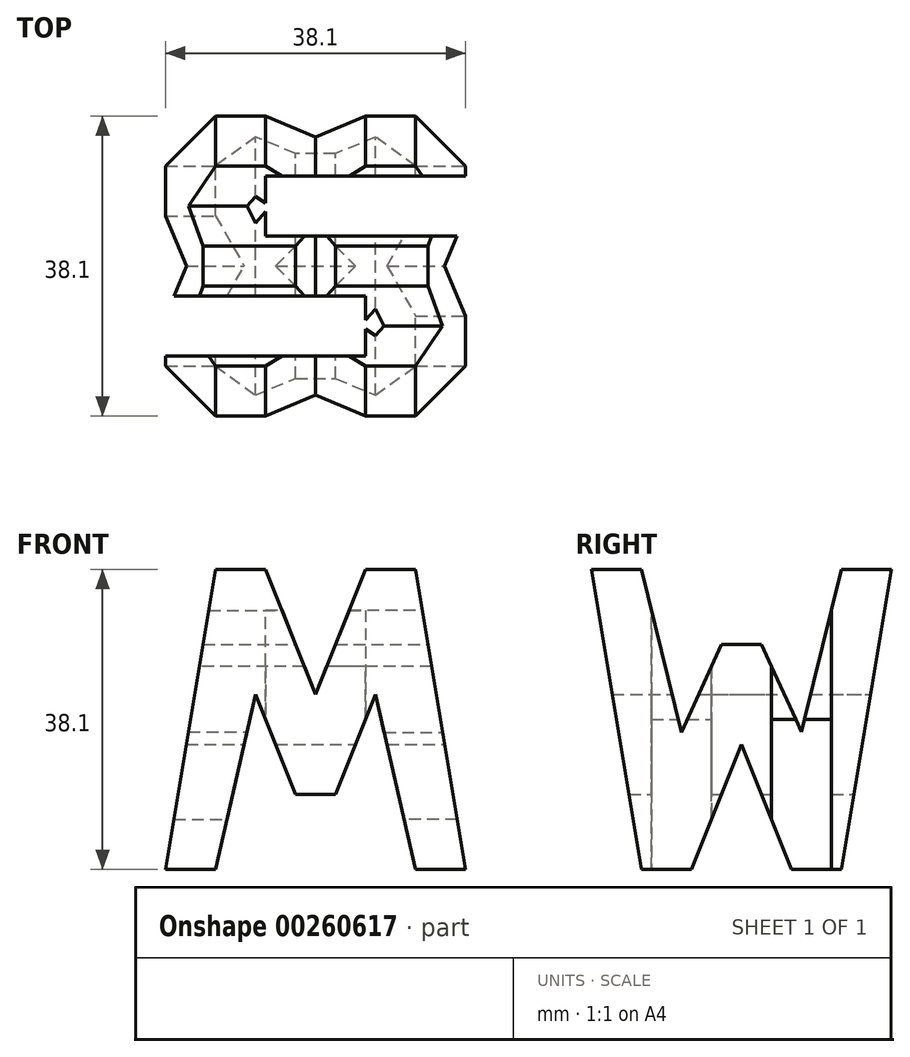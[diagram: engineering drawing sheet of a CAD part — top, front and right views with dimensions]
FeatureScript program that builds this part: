
annotation { "Feature Type Name" : "Feature", "Feature Type Description" : "" }
export const myFeature = defineFeature(function(context is Context, id is Id, definition is map)
    precondition{}
    {
        {
            var Q0;
            Q0=qCreatedBy(makeId("Front.planeOp"),FACE);
            var sketch = newSketch(context, id + "F0", { "sketchPlane" : qUnion([Q0])});
            skLineSegment(sketch, "E0", {"start": v(0, 0) * mm, "end": v(38.1, 0) * mm});
            skLineSegment(sketch, "E1", {"start": v(38.1, 0) * mm, "end": v(38.1, 38.1) * mm});
            skLineSegment(sketch, "E2", {"start": v(38.1, 38.1) * mm, "end": v(0, 38.1) * mm});
            skLineSegment(sketch, "E3", {"start": v(0, 38.1) * mm, "end": v(0, 0) * mm});
            skLineSegment(sketch, "E4", {"start": v(38.1, 0) * mm, "end": v(31.75, 38.1) * mm});
            skLineSegment(sketch, "E5", {"start": v(25.4, 38.1) * mm, "end": v(19.05, 22.22) * mm});
            skPoint(sketch, "E5.endSnap0", {"position": v(19.05, 38.1) * mm});
            skLineSegment(sketch, "E6", {"start": v(19.05, 22.22) * mm, "end": v(12.7, 38.1) * mm});
            skLineSegment(sketch, "E7", {"start": v(0, 0) * mm, "end": v(6.35, 38.1) * mm});
            skLineSegment(sketch, "E8", {"start": v(31.75, 0) * mm, "end": v(26.67, 22.23) * mm});
            skLineSegment(sketch, "E9", {"start": v(26.67, 22.23) * mm, "end": v(21.6, 9.52) * mm});
            skLineSegment(sketch, "E10", {"start": v(21.59, 9.52) * mm, "end": v(16.51, 9.52) * mm});
            skLineSegment(sketch, "E11", {"start": v(16.5, 9.53) * mm, "end": v(11.43, 22.22) * mm});
            skLineSegment(sketch, "E12", {"start": v(11.43, 22.23) * mm, "end": v(6.35, 0) * mm});
            skSolve(sketch);
        }
        {
            var Q0;
            Q0 = qSketchRegion(id + "F0", true);
            extrude(context, id + "F1", {"entities" : qUnion([Q0]), "depth" : 38.1 * mm});
        }
        {
            var Q0;
            Q0=qCreatedBy(makeId("Right.planeOp"),FACE);
            cPlane(context, id + "F2", {"entities" : qUnion([Q0]), "cplaneType" : CPlaneType.OFFSET, "offset" : 38.1 * mm, "width" : 152.4 * mm, "height" : 152.4 * mm});
        }
        {
            var Q0;
            Q0=qCreatedBy(makeId("Top.planeOp"),FACE);
            cPlane(context, id + "F3", {"entities" : qUnion([Q0]), "cplaneType" : CPlaneType.OFFSET, "offset" : 38.1 * mm, "width" : 152.4 * mm, "height" : 152.4 * mm});
        }
        {
            var Q0;
            Q0=qCreatedBy(id+"F2.planeOp",FACE);
            var sketch = newSketch(context, id + "F4", { "sketchPlane" : qUnion([Q0])});
            skLineSegment(sketch, "E13", {"start": v(0, 0) * mm, "end": v(0, 38.1) * mm});
            skLineSegment(sketch, "E14", {"start": v(0, 38.1) * mm, "end": v(-38.1, 38.1) * mm});
            skLineSegment(sketch, "E15", {"start": v(-38.1, 38.1) * mm, "end": v(-38.1, 0) * mm});
            skLineSegment(sketch, "E16", {"start": v(-38.1, 0) * mm, "end": v(0, 0) * mm});
            skLineSegment(sketch, "E17", {"start": v(-38.1, 38.1) * mm, "end": v(-31.75, 0) * mm});
            skLineSegment(sketch, "E18", {"start": v(-6.35, 0) * mm, "end": v(0, 38.1) * mm});
            skLineSegment(sketch, "E19", {"start": v(-31.75, 38.1) * mm, "end": v(-26.67, 17.42) * mm});
            skLineSegment(sketch, "E20", {"start": v(-26.67, 17.42) * mm, "end": v(-21.59, 28.58) * mm});
            skLineSegment(sketch, "E21", {"start": v(-21.59, 28.58) * mm, "end": v(-16.5, 28.58) * mm});
            skLineSegment(sketch, "E22", {"start": v(-16.5, 28.58) * mm, "end": v(-11.43, 17.45) * mm});
            skLineSegment(sketch, "E23", {"start": v(-11.43, 17.45) * mm, "end": v(-6.35, 38.1) * mm});
            skLineSegment(sketch, "E24", {"start": v(-19.05, 15.88) * mm, "end": v(-25.4, 0) * mm});
            skPoint(sketch, "E24.startSnap0", {"position": v(-19.05, 28.58) * mm});
            skLineSegment(sketch, "E25", {"start": v(-19.05, 15.88) * mm, "end": v(-12.7, 0) * mm});
            skSolve(sketch);
        }
        {
            var Q0;
            {var subQ0=sQuery(id+"F4.wireOp",EDGE,"E15");Q0=makeQuery(id+"F4.imprint","IMPRINT",FACE,{"disambiguationData":[TD([[makeQuery(id+"F4.imprint","IMPRINT",EDGE,{"derivedFrom":subQ0}),1.0]])]});}
            var Q1;
            {var subQ0=sQuery(id+"F4.wireOp",EDGE,"E19");Q1=makeQuery(id+"F4.imprint","IMPRINT",FACE,{"disambiguationData":[TD([[makeQuery(id+"F4.imprint","IMPRINT",EDGE,{"derivedFrom":subQ0}),1.0]])]});}
            var Q2;
            {var subQ0=sQuery(id+"F4.wireOp",EDGE,"E24");Q2=makeQuery(id+"F4.imprint","IMPRINT",FACE,{"disambiguationData":[TD([[makeQuery(id+"F4.imprint","IMPRINT",EDGE,{"derivedFrom":subQ0}),1.0]])]});}
            var Q3;
            {var subQ0=sQuery(id+"F4.wireOp",EDGE,"E13");Q3=makeQuery(id+"F4.imprint","IMPRINT",FACE,{"disambiguationData":[TD([[makeQuery(id+"F4.imprint","IMPRINT",EDGE,{"derivedFrom":subQ0}),1.0]])]});}
            extrude(context, id + "F5", {"entities" : qUnion([Q0, Q1, Q2, Q3]), "operationType" : NewBodyOperationType.REMOVE, "oppositeDirection" : true, "depth" : 38.1 * mm});
        }
        {
            var Q0;
            {var subQ0=sQuery(id+"F0.wireOp",EDGE,"E1");Q0=makeQuery(id+"F0.imprint","IMPRINT",FACE,{"disambiguationData":[TD([[makeQuery(id+"F0.imprint","IMPRINT",EDGE,{"derivedFrom":subQ0}),1.0]])]});}
            var Q1;
            {var subQ0=sQuery(id+"F0.wireOp",EDGE,"E5");Q1=makeQuery(id+"F0.imprint","IMPRINT",FACE,{"disambiguationData":[TD([[makeQuery(id+"F0.imprint","IMPRINT",EDGE,{"derivedFrom":subQ0}),-1.0]])]});}
            var Q2;
            {var subQ0=sQuery(id+"F0.wireOp",EDGE,"E3");Q2=makeQuery(id+"F0.imprint","IMPRINT",FACE,{"disambiguationData":[TD([[makeQuery(id+"F0.imprint","IMPRINT",EDGE,{"derivedFrom":subQ0}),1.0]])]});}
            var Q3;
            {var subQ0=sQuery(id+"F0.wireOp",EDGE,"E8");Q3=makeQuery(id+"F0.imprint","IMPRINT",FACE,{"disambiguationData":[TD([[makeQuery(id+"F0.imprint","IMPRINT",EDGE,{"derivedFrom":subQ0}),1.0]])]});}
            extrude(context, id + "F6", {"entities" : qUnion([Q0, Q1, Q2, Q3]), "operationType" : NewBodyOperationType.REMOVE, "depth" : 38.1 * mm});
        }
        {
            var Q0;
            Q0=qCreatedBy(id+"F3.planeOp",FACE);
            var sketch = newSketch(context, id + "F7", { "sketchPlane" : qUnion([Q0])});
            skLineSegment(sketch, "E26", {"start": v(0, 0) * mm, "end": v(38.1, 0) * mm});
            skLineSegment(sketch, "E27", {"start": v(38.1, 0) * mm, "end": v(38.1, -38.1) * mm});
            skLineSegment(sketch, "E28", {"start": v(38.1, -38.1) * mm, "end": v(0, -38.1) * mm});
            skLineSegment(sketch, "E29", {"start": v(0, -38.1) * mm, "end": v(0, 0) * mm});
            skLineSegment(sketch, "E30", {"start": v(12.7, -7.62) * mm, "end": v(12.7, -15.24) * mm});
            skLineSegment(sketch, "E31", {"start": v(12.7, -15.24) * mm, "end": v(38.1, -15.24) * mm});
            skLineSegment(sketch, "E32", {"start": v(38.1, -15.24) * mm, "end": v(38.1, -7.62) * mm});
            skLineSegment(sketch, "E33", {"start": v(38.1, -7.62) * mm, "end": v(12.7, -7.62) * mm});
            skLineSegment(sketch, "E34", {"start": v(0, -22.86) * mm, "end": v(25.4, -22.86) * mm});
            skLineSegment(sketch, "E35", {"start": v(25.4, -22.86) * mm, "end": v(25.4, -30.48) * mm});
            skLineSegment(sketch, "E36", {"start": v(25.4, -30.48) * mm, "end": v(0, -30.48) * mm});
            skLineSegment(sketch, "E37", {"start": v(0, -30.48) * mm, "end": v(0, -22.86) * mm});
            skSolve(sketch);
        }
        {
            var Q0;
            Q0=makeQuery(id+"F7.imprint","IMPRINT",FACE,{"disambiguationData":[TD([[makeQuery(id+"F7.imprint","IMPRINT",EDGE,{"derivedFrom":sQuery(id+"F7.wireOp",EDGE,"E34")}),-1.0]])]});
            var Q1;
            Q1=makeQuery(id+"F7.imprint","IMPRINT",FACE,{"disambiguationData":[TD([[makeQuery(id+"F7.imprint","IMPRINT",EDGE,{"derivedFrom":sQuery(id+"F7.wireOp",EDGE,"E30")}),1.0]])]});
            extrude(context, id + "F8", {"entities" : qUnion([Q0, Q1]), "operationType" : NewBodyOperationType.REMOVE, "oppositeDirection" : true, "depth" : 38.1 * mm});
        }
    });
